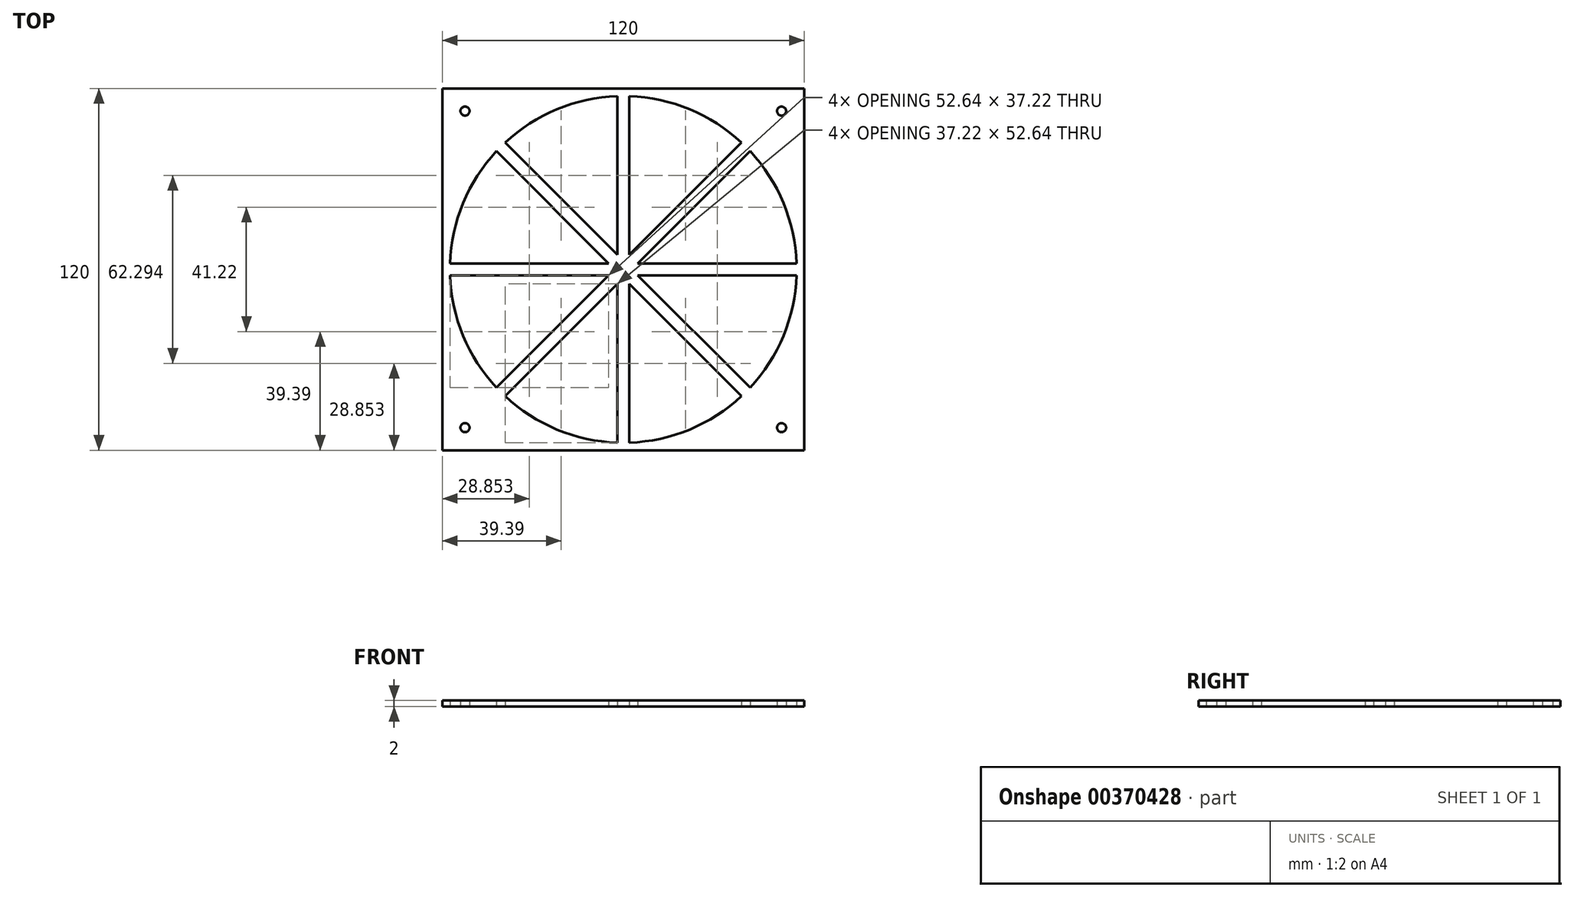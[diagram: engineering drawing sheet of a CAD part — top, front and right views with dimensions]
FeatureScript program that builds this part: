
annotation { "Feature Type Name" : "Feature", "Feature Type Description" : "" }
export const myFeature = defineFeature(function(context is Context, id is Id, definition is map)
    precondition{}
    {
        {
            var Q0;
            Q0=qCreatedBy(makeId("Top.planeOp"),FACE);
            var sketch = newSketch(context, id + "F0", { "sketchPlane" : qUnion([Q0])});
            skLineSegment(sketch, "E0.bottom", {"start": v(60, -60) * mm, "end": v(-60, -60) * mm});
            skLineSegment(sketch, "E0.top", {"start": v(60, 60) * mm, "end": v(-60, 60) * mm});
            skLineSegment(sketch, "E0.left", {"start": v(60, -60) * mm, "end": v(60, 60) * mm});
            skLineSegment(sketch, "E0.right", {"start": v(-60, -60) * mm, "end": v(-60, 60) * mm});
            skPoint(sketch, "E0.middle", {"position": v(0, 0) * mm});
            skCircle(sketch, "E1", {"center": v(0, 0) * mm, "radius": 57.5 * mm});
            skPoint(sketch, "E2", {"position": v(52.5, 52.5) * mm});
            skPoint(sketch, "E3", {"position": v(-52.5, 52.5) * mm});
            skPoint(sketch, "E4", {"position": v(-52.5, -52.5) * mm});
            skPoint(sketch, "E5", {"position": v(52.5, -52.5) * mm});
            skLineSegment(sketch, "E6", {"start": v(57.47, 2) * mm, "end": v(0, 2) * mm});
            skLineSegment(sketch, "E7", {"start": v(57.47, -2) * mm, "end": v(0, -2) * mm});
            skLineSegment(sketch, "E8", {"start": v(0, -2) * mm, "end": v(0, 0) * mm});
            skLineSegment(sketch, "E9", {"start": v(0, 2) * mm, "end": v(0, 0) * mm});
            skLineSegment(sketch, "E10.1.0", {"start": v(42.05, 39.22) * mm, "end": v(1.41, -1.41) * mm});
            skLineSegment(sketch, "E10.1.1", {"start": v(39.22, 42.05) * mm, "end": v(-1.41, 1.41) * mm});
            skLineSegment(sketch, "E10.2.0", {"start": v(2, 57.47) * mm, "end": v(2, 0) * mm});
            skLineSegment(sketch, "E10.2.1", {"start": v(-2, 57.47) * mm, "end": v(-2, 0) * mm});
            skLineSegment(sketch, "E10.3.0", {"start": v(-39.22, 42.05) * mm, "end": v(1.41, 1.41) * mm});
            skLineSegment(sketch, "E10.3.1", {"start": v(-42.05, 39.22) * mm, "end": v(-1.41, -1.41) * mm});
            skLineSegment(sketch, "E10.4.0", {"start": v(-57.47, 2) * mm, "end": v(0, 2) * mm});
            skLineSegment(sketch, "E10.4.1", {"start": v(-57.47, -2) * mm, "end": v(0, -2) * mm});
            skLineSegment(sketch, "E10.5.0", {"start": v(-42.05, -39.22) * mm, "end": v(-1.41, 1.41) * mm});
            skLineSegment(sketch, "E10.5.1", {"start": v(-39.22, -42.05) * mm, "end": v(1.41, -1.41) * mm});
            skLineSegment(sketch, "E10.6.0", {"start": v(-2, -57.47) * mm, "end": v(-2, 0) * mm});
            skLineSegment(sketch, "E10.6.1", {"start": v(2, -57.47) * mm, "end": v(2, 0) * mm});
            skLineSegment(sketch, "E10.7.0", {"start": v(39.22, -42.05) * mm, "end": v(-1.41, -1.41) * mm});
            skLineSegment(sketch, "E10.7.1", {"start": v(42.05, -39.22) * mm, "end": v(1.41, 1.41) * mm});
            skSolve(sketch);
        }
        {
            var Q0;
            Q0=makeQuery(id+"F0.imprint","IMPRINT",FACE,{"disambiguationData":[TD([[makeQuery(id+"F0.imprint","IMPRINT",EDGE,{"derivedFrom":sQuery(id+"F0.wireOp",EDGE,"E0.bottom")}),-1.0]])]});
            var Q1;
            {var subQ1=sQuery(id+"F0.wireOp",EDGE,"E1");var subQ5=sQuery(id+"F0.wireOp",EDGE,"E10.3.0");var subQ6=makeQuery(id+"F0.imprint","INTERSECT",VERTEX,{"derivedFrom":[subQ1,subQ5]});Q1=makeQuery(id+"F0.imprint","IMPRINT",FACE,{"disambiguationData":[TD([[makeQuery(id+"F0.imprint","IMPRINT",EDGE,{"disambiguationData":[TD([[subQ6,-1.0]])],"derivedFrom":subQ1}),1.0]])]});}
            var Q2;
            {var subQ0=sQuery(id+"F0.wireOp",EDGE,"E10.2.0");var subQ1=sQuery(id+"F0.wireOp",EDGE,"E1");var subQ2=makeQuery(id+"F0.imprint","INTERSECT",VERTEX,{"derivedFrom":[subQ1,subQ0]});Q2=makeQuery(id+"F0.imprint","IMPRINT",FACE,{"disambiguationData":[TD([[makeQuery(id+"F0.imprint","IMPRINT",EDGE,{"disambiguationData":[TD([[subQ2,-1.0]])],"derivedFrom":subQ1}),1.0]])]});}
            var Q3;
            {var subQ1=sQuery(id+"F0.wireOp",EDGE,"E1");var subQ5=sQuery(id+"F0.wireOp",EDGE,"E10.4.0");var subQ6=makeQuery(id+"F0.imprint","INTERSECT",VERTEX,{"derivedFrom":[subQ1,subQ5]});Q3=makeQuery(id+"F0.imprint","IMPRINT",FACE,{"disambiguationData":[TD([[makeQuery(id+"F0.imprint","IMPRINT",EDGE,{"disambiguationData":[TD([[subQ6,-1.0]])],"derivedFrom":subQ1}),1.0]])]});}
            var Q4;
            {var subQ1=sQuery(id+"F0.wireOp",EDGE,"E1");var subQ5=sQuery(id+"F0.wireOp",EDGE,"E10.5.0");var subQ6=makeQuery(id+"F0.imprint","INTERSECT",VERTEX,{"derivedFrom":[subQ1,subQ5]});Q4=makeQuery(id+"F0.imprint","IMPRINT",FACE,{"disambiguationData":[TD([[makeQuery(id+"F0.imprint","IMPRINT",EDGE,{"disambiguationData":[TD([[subQ6,-1.0]])],"derivedFrom":subQ1}),1.0]])]});}
            var Q5;
            {var subQ1=sQuery(id+"F0.wireOp",EDGE,"E1");var subQ5=sQuery(id+"F0.wireOp",EDGE,"E10.6.0");var subQ9=makeQuery(id+"F0.imprint","INTERSECT",VERTEX,{"derivedFrom":[subQ1,subQ5]});Q5=makeQuery(id+"F0.imprint","IMPRINT",FACE,{"disambiguationData":[TD([[makeQuery(id+"F0.imprint","IMPRINT",EDGE,{"disambiguationData":[TD([[subQ9,-1.0]])],"derivedFrom":subQ1}),1.0]])]});}
            var Q6;
            {var subQ0=sQuery(id+"F0.wireOp",EDGE,"E10.7.0");var subQ1=sQuery(id+"F0.wireOp",EDGE,"E1");var subQ2=makeQuery(id+"F0.imprint","INTERSECT",VERTEX,{"derivedFrom":[subQ1,subQ0]});Q6=makeQuery(id+"F0.imprint","IMPRINT",FACE,{"disambiguationData":[TD([[makeQuery(id+"F0.imprint","IMPRINT",EDGE,{"disambiguationData":[TD([[subQ2,-1.0]])],"derivedFrom":subQ1}),1.0]])]});}
            var Q7;
            {var subQ1=sQuery(id+"F0.wireOp",EDGE,"E6");var subQ5=sQuery(id+"F0.wireOp",EDGE,"E1");var subQ6=makeQuery(id+"F0.imprint","INTERSECT",VERTEX,{"derivedFrom":[subQ5,subQ1]});Q7=makeQuery(id+"F0.imprint","IMPRINT",FACE,{"disambiguationData":[TD([[makeQuery(id+"F0.imprint","IMPRINT",EDGE,{"disambiguationData":[TD([[subQ6,1.0]])],"derivedFrom":subQ5}),1.0]])]});}
            var Q8;
            {var subQ1=sQuery(id+"F0.wireOp",EDGE,"E1");var subQ5=sQuery(id+"F0.wireOp",EDGE,"E10.1.0");var subQ9=makeQuery(id+"F0.imprint","INTERSECT",VERTEX,{"derivedFrom":[subQ1,subQ5]});Q8=makeQuery(id+"F0.imprint","IMPRINT",FACE,{"disambiguationData":[TD([[makeQuery(id+"F0.imprint","IMPRINT",EDGE,{"disambiguationData":[TD([[subQ9,-1.0]])],"derivedFrom":subQ1}),1.0]])]});}
            var Q9;
            {var subQ0=sQuery(id+"F0.wireOp",EDGE,"E10.1.0");var subQ1=sQuery(id+"F0.wireOp",EDGE,"E6");var subQ2=makeQuery(id+"F0.imprint","INTERSECT",VERTEX,{"derivedFrom":[subQ1,subQ0]});Q9=makeQuery(id+"F0.imprint","IMPRINT",FACE,{"disambiguationData":[TD([[makeQuery(id+"F0.imprint","IMPRINT",EDGE,{"disambiguationData":[TD([[subQ2,-1.0]])],"derivedFrom":subQ1}),1.0]])]});}
            var Q10;
            {var subQ0=sQuery(id+"F0.wireOp",EDGE,"E10.2.0");var subQ1=sQuery(id+"F0.wireOp",EDGE,"E6");var subQ2=makeQuery(id+"F0.imprint","INTERSECT",VERTEX,{"derivedFrom":[subQ1,subQ0]});Q10=makeQuery(id+"F0.imprint","IMPRINT",FACE,{"disambiguationData":[TD([[makeQuery(id+"F0.imprint","IMPRINT",EDGE,{"disambiguationData":[TD([[subQ2,-1.0]])],"derivedFrom":subQ1}),-1.0]])]});}
            var Q11;
            {var subQ0=sQuery(id+"F0.wireOp",EDGE,"E10.3.0");var subQ1=sQuery(id+"F0.wireOp",EDGE,"E10.1.1");var subQ2=makeQuery(id+"F0.imprint","INTERSECT",VERTEX,{"derivedFrom":[subQ1,subQ0]});Q11=makeQuery(id+"F0.imprint","IMPRINT",FACE,{"disambiguationData":[TD([[makeQuery(id+"F0.imprint","IMPRINT",EDGE,{"disambiguationData":[TD([[subQ2,-1.0]])],"derivedFrom":subQ1}),-1.0]])]});}
            var Q12;
            {var subQ0=sQuery(id+"F0.wireOp",EDGE,"E10.4.0");var subQ1=sQuery(id+"F0.wireOp",EDGE,"E10.2.1");var subQ2=makeQuery(id+"F0.imprint","INTERSECT",VERTEX,{"derivedFrom":[subQ1,subQ0]});Q12=makeQuery(id+"F0.imprint","IMPRINT",FACE,{"disambiguationData":[TD([[makeQuery(id+"F0.imprint","IMPRINT",EDGE,{"disambiguationData":[TD([[subQ2,-1.0]])],"derivedFrom":subQ1}),-1.0]])]});}
            var Q13;
            {var subQ0=sQuery(id+"F0.wireOp",EDGE,"E10.5.0");var subQ1=sQuery(id+"F0.wireOp",EDGE,"E10.3.1");var subQ2=makeQuery(id+"F0.imprint","INTERSECT",VERTEX,{"derivedFrom":[subQ1,subQ0]});Q13=makeQuery(id+"F0.imprint","IMPRINT",FACE,{"disambiguationData":[TD([[makeQuery(id+"F0.imprint","IMPRINT",EDGE,{"disambiguationData":[TD([[subQ2,-1.0]])],"derivedFrom":subQ1}),-1.0]])]});}
            var Q14;
            {var subQ0=sQuery(id+"F0.wireOp",EDGE,"E10.6.0");var subQ1=sQuery(id+"F0.wireOp",EDGE,"E10.4.1");var subQ2=makeQuery(id+"F0.imprint","INTERSECT",VERTEX,{"derivedFrom":[subQ1,subQ0]});Q14=makeQuery(id+"F0.imprint","IMPRINT",FACE,{"disambiguationData":[TD([[makeQuery(id+"F0.imprint","IMPRINT",EDGE,{"disambiguationData":[TD([[subQ2,-1.0]])],"derivedFrom":subQ1}),-1.0]])]});}
            var Q15;
            {var subQ0=sQuery(id+"F0.wireOp",EDGE,"E10.7.0");var subQ1=sQuery(id+"F0.wireOp",EDGE,"E10.3.1");var subQ2=makeQuery(id+"F0.imprint","INTERSECT",VERTEX,{"derivedFrom":[subQ1,subQ0]});Q15=makeQuery(id+"F0.imprint","IMPRINT",FACE,{"disambiguationData":[TD([[makeQuery(id+"F0.imprint","IMPRINT",EDGE,{"disambiguationData":[TD([[subQ2,1.0]])],"derivedFrom":subQ1}),-1.0]])]});}
            var Q16;
            {var subQ16=sQuery(id+"F0.wireOp",EDGE,"E8");Q16=makeQuery(id+"F0.imprint","IMPRINT",FACE,{"disambiguationData":[TD([[makeQuery(id+"F0.imprint","IMPRINT",EDGE,{"derivedFrom":subQ16}),1.0]])]});}
            var Q17;
            {var subQ0=sQuery(id+"F0.wireOp",EDGE,"E10.6.0");var subQ1=sQuery(id+"F0.wireOp",EDGE,"E10.2.1");var subQ2=makeQuery(id+"F0.imprint","INTERSECT",VERTEX,{"derivedFrom":[subQ1,subQ0]});Q17=makeQuery(id+"F0.imprint","IMPRINT",FACE,{"disambiguationData":[TD([[makeQuery(id+"F0.imprint","IMPRINT",EDGE,{"disambiguationData":[TD([[subQ2,1.0]])],"derivedFrom":subQ1}),-1.0]])]});}
            var Q18;
            {var subQ0=sQuery(id+"F0.wireOp",EDGE,"E10.5.0");var subQ1=sQuery(id+"F0.wireOp",EDGE,"E10.1.1");var subQ2=makeQuery(id+"F0.imprint","INTERSECT",VERTEX,{"derivedFrom":[subQ1,subQ0]});Q18=makeQuery(id+"F0.imprint","IMPRINT",FACE,{"disambiguationData":[TD([[makeQuery(id+"F0.imprint","IMPRINT",EDGE,{"disambiguationData":[TD([[subQ2,1.0]])],"derivedFrom":subQ1}),-1.0]])]});}
            var Q19;
            {var subQ3=sQuery(id+"F0.wireOp",EDGE,"E10.3.0");var subQ5=sQuery(id+"F0.wireOp",EDGE,"E10.1.1");var subQ6=makeQuery(id+"F0.imprint","INTERSECT",VERTEX,{"derivedFrom":[subQ5,subQ3]});Q19=makeQuery(id+"F0.imprint","IMPRINT",FACE,{"disambiguationData":[TD([[makeQuery(id+"F0.imprint","IMPRINT",EDGE,{"disambiguationData":[TD([[subQ6,-1.0]])],"derivedFrom":subQ5}),1.0]])]});}
            var Q20;
            {var subQ1=sQuery(id+"F0.wireOp",EDGE,"E8");Q20=makeQuery(id+"F0.imprint","IMPRINT",FACE,{"disambiguationData":[TD([[makeQuery(id+"F0.imprint","IMPRINT",EDGE,{"derivedFrom":subQ1}),-1.0]])]});}
            var Q21;
            {var subQ0=sQuery(id+"F0.wireOp",EDGE,"E10.2.0");var subQ1=sQuery(id+"F0.wireOp",EDGE,"E6");var subQ2=makeQuery(id+"F0.imprint","INTERSECT",VERTEX,{"derivedFrom":[subQ1,subQ0]});Q21=makeQuery(id+"F0.imprint","IMPRINT",FACE,{"disambiguationData":[TD([[makeQuery(id+"F0.imprint","IMPRINT",EDGE,{"disambiguationData":[TD([[subQ2,-1.0]])],"derivedFrom":subQ1}),1.0]])]});}
            var Q22;
            {var subQ0=sQuery(id+"F0.wireOp",EDGE,"E10.7.1");var subQ1=sQuery(id+"F0.wireOp",EDGE,"E7");var subQ2=makeQuery(id+"F0.imprint","INTERSECT",VERTEX,{"derivedFrom":[subQ1,subQ0]});Q22=makeQuery(id+"F0.imprint","IMPRINT",FACE,{"disambiguationData":[TD([[makeQuery(id+"F0.imprint","IMPRINT",EDGE,{"disambiguationData":[TD([[subQ2,-1.0]])],"derivedFrom":subQ1}),-1.0]])]});}
            var Q23;
            {var subQ0=sQuery(id+"F0.wireOp",EDGE,"E10.6.1");var subQ1=sQuery(id+"F0.wireOp",EDGE,"E7");var subQ2=makeQuery(id+"F0.imprint","INTERSECT",VERTEX,{"derivedFrom":[subQ1,subQ0]});Q23=makeQuery(id+"F0.imprint","IMPRINT",FACE,{"disambiguationData":[TD([[makeQuery(id+"F0.imprint","IMPRINT",EDGE,{"disambiguationData":[TD([[subQ2,-1.0]])],"derivedFrom":subQ1}),1.0]])]});}
            var Q24;
            {var subQ1=sQuery(id+"F0.wireOp",EDGE,"E7");var subQ3=sQuery(id+"F0.wireOp",EDGE,"E10.5.1");var subQ4=makeQuery(id+"F0.imprint","INTERSECT",VERTEX,{"derivedFrom":[subQ1,subQ3]});Q24=makeQuery(id+"F0.imprint","IMPRINT",FACE,{"disambiguationData":[TD([[makeQuery(id+"F0.imprint","IMPRINT",EDGE,{"disambiguationData":[TD([[subQ4,1.0]])],"derivedFrom":subQ3}),1.0]])]});}
            var Q25;
            {var subQ0=sQuery(id+"F0.wireOp",EDGE,"E10.7.1");var subQ1=sQuery(id+"F0.wireOp",EDGE,"E10.1.0");var subQ2=makeQuery(id+"F0.imprint","INTERSECT",VERTEX,{"derivedFrom":[subQ1,subQ0]});Q25=makeQuery(id+"F0.imprint","IMPRINT",FACE,{"disambiguationData":[TD([[makeQuery(id+"F0.imprint","IMPRINT",EDGE,{"disambiguationData":[TD([[subQ2,-1.0]])],"derivedFrom":subQ1}),-1.0]])]});}
            var Q26;
            {var subQ0=sQuery(id+"F0.wireOp",EDGE,"E10.6.1");var subQ1=sQuery(id+"F0.wireOp",EDGE,"E7");var subQ2=makeQuery(id+"F0.imprint","INTERSECT",VERTEX,{"derivedFrom":[subQ1,subQ0]});Q26=makeQuery(id+"F0.imprint","IMPRINT",FACE,{"disambiguationData":[TD([[makeQuery(id+"F0.imprint","IMPRINT",EDGE,{"disambiguationData":[TD([[subQ2,-1.0]])],"derivedFrom":subQ1}),-1.0]])]});}
            extrude(context, id + "F1", {"entities" : qUnion([Q0, Q1, Q2, Q3, Q4, Q5, Q6, Q7, Q8, Q9, Q10, Q11, Q12, Q13, Q14, Q15, Q16, Q17, Q18, Q19, Q20, Q21, Q22, Q23, Q24, Q25, Q26]), "depth" : 2 * mm});
        }
        {
            var Q0;
            Q0=sQuery(id+"F0.wireOp",VERTEX,"E3");
            var Q1;
            Q1=sQuery(id+"F0.wireOp",VERTEX,"E4");
            var Q2;
            Q2=sQuery(id+"F0.wireOp",VERTEX,"E5");
            var Q3;
            Q3=sQuery(id+"F0.wireOp",VERTEX,"E2");
            var Q4;
            Q4=makeQuery(id+"F1.opExtrude","SWEPT_BODY",BODY,{"disambiguationData":[OSD([sQuery(id+"F0.wireOp",EDGE,"E0.bottom"),sQuery(id+"F0.wireOp",EDGE,"E0.top"),sQuery(id+"F0.wireOp",EDGE,"E0.left"),sQuery(id+"F0.wireOp",EDGE,"E0.right"),sQuery(id+"F0.wireOp",EDGE,"E1"),sQuery(id+"F0.wireOp",EDGE,"E6"),sQuery(id+"F0.wireOp",EDGE,"E7"),sQuery(id+"F0.wireOp",EDGE,"E10.1.0"),sQuery(id+"F0.wireOp",EDGE,"E10.1.1"),sQuery(id+"F0.wireOp",EDGE,"E10.2.0"),sQuery(id+"F0.wireOp",EDGE,"E10.2.1"),sQuery(id+"F0.wireOp",EDGE,"E10.3.0"),sQuery(id+"F0.wireOp",EDGE,"E10.3.1"),sQuery(id+"F0.wireOp",EDGE,"E10.4.0"),sQuery(id+"F0.wireOp",EDGE,"E10.4.1"),sQuery(id+"F0.wireOp",EDGE,"E10.5.0"),sQuery(id+"F0.wireOp",EDGE,"E10.5.1"),sQuery(id+"F0.wireOp",EDGE,"E10.6.0"),sQuery(id+"F0.wireOp",EDGE,"E10.6.1"),sQuery(id+"F0.wireOp",EDGE,"E10.7.0"),sQuery(id+"F0.wireOp",EDGE,"E10.7.1")])]});
            hole(context, id + "F2", {"style" : HoleStyle.SIMPLE, "endStyle" : HoleEndStyle.THROUGH, "oppositeDirection" : true, "holeDiameter" : 3 * mm, "isTappedThrough" : true, "tappedDepth" : 12 * mm, "tapClearance" : 3, "locations" : qUnion([Q0, Q1, Q2, Q3]), "scope" : qUnion([Q4])});
        }
    });
